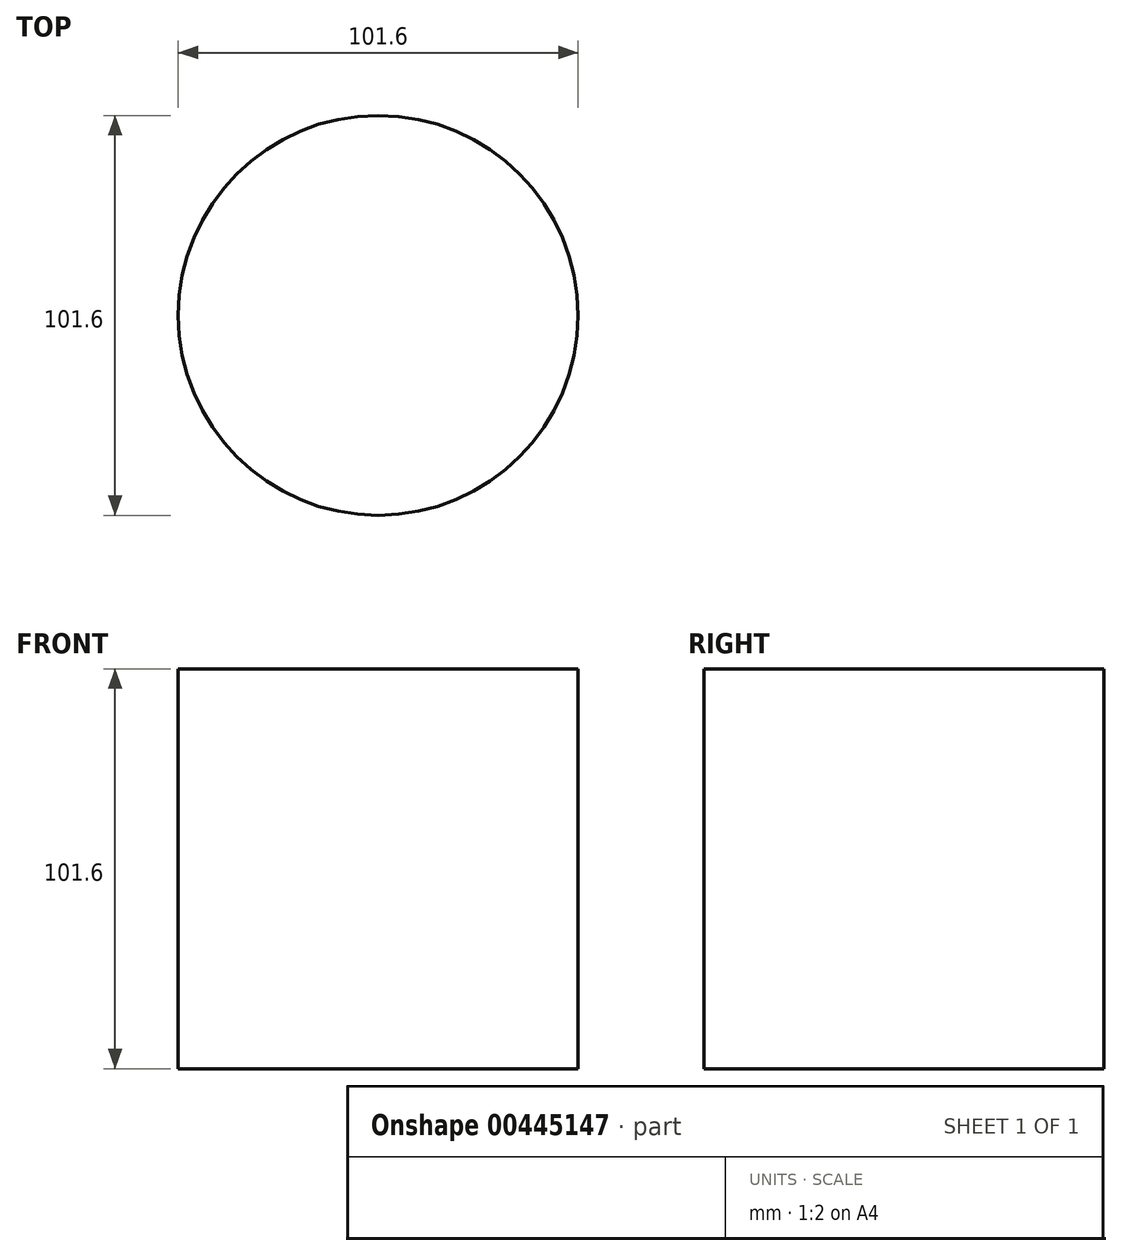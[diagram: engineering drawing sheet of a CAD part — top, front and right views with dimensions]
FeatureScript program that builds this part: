
annotation { "Feature Type Name" : "Feature", "Feature Type Description" : "" }
export const myFeature = defineFeature(function(context is Context, id is Id, definition is map)
    precondition{}
    {
        {
            var Q0;
            Q0=qCreatedBy(makeId("Top.planeOp"),FACE);
            var sketch = newSketch(context, id + "F0", { "sketchPlane" : qUnion([Q0])});
            skCircle(sketch, "E0", {"center": v(0, 0) * mm, "radius": 50.8 * mm});
            skSolve(sketch);
        }
        {
            var Q0;
            Q0=makeQuery(id+"F0.imprint","IMPRINT",FACE,{"disambiguationData":[TD([[makeQuery(id+"F0.imprint","IMPRINT",EDGE,{"derivedFrom":sQuery(id+"F0.wireOp",EDGE,"E0")}),1.0]])]});
            extrude(context, id + "F1", {"entities" : qUnion([Q0]), "depth" : 101.6 * mm});
        }
    });
